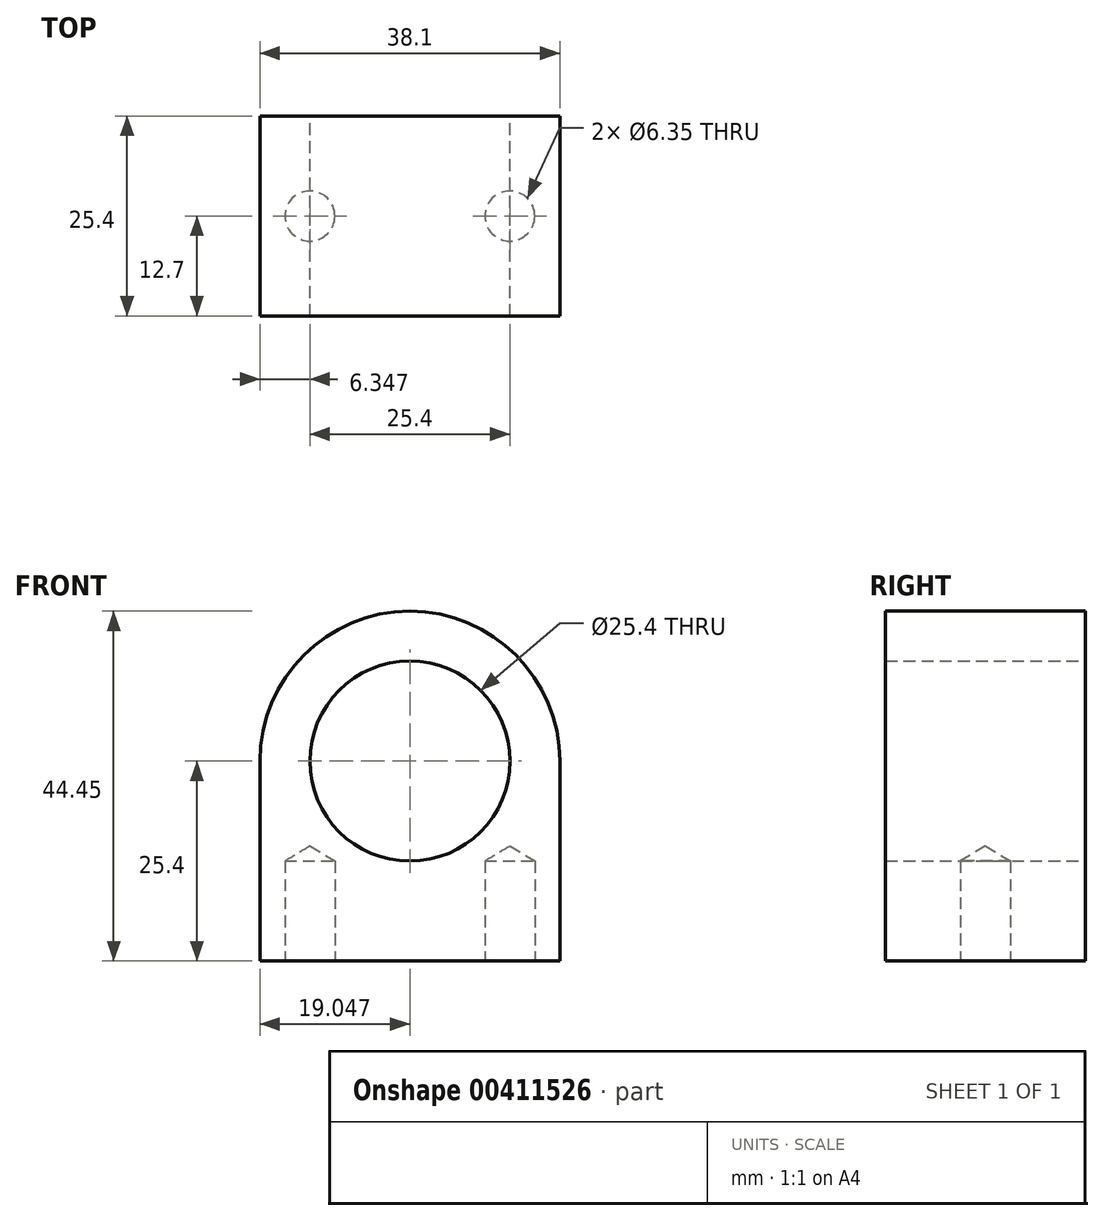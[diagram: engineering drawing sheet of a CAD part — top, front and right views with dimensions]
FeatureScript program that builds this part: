
annotation { "Feature Type Name" : "Feature", "Feature Type Description" : "" }
export const myFeature = defineFeature(function(context is Context, id is Id, definition is map)
    precondition{}
    {
        {
            var Q0;
            Q0=qCreatedBy(makeId("Front.planeOp"),FACE);
            var sketch = newSketch(context, id + "F0", { "sketchPlane" : qUnion([Q0])});
            skLineSegment(sketch, "E0", {"start": v(-22.9, 0) * mm, "end": v(-22.9, -25.4) * mm});
            skLineSegment(sketch, "E1", {"start": v(-22.9, -25.4) * mm, "end": v(15.2, -25.4) * mm});
            skLineSegment(sketch, "E2", {"start": v(15.2, -25.4) * mm, "end": v(15.2, 0) * mm});
            skArc(sketch, "E3", {"start": v(15.2, 0) * mm, "mid": v(-3.84, 19.05) * mm, "end": v(-22.9, 0) * mm});
            skPoint(sketch, "E3.centerSnap0", {"position": v(-3.84, -25.4) * mm});
            skCircle(sketch, "E4", {"center": v(-3.84, 0) * mm, "radius": 12.7 * mm});
            skSolve(sketch);
        }
        {
            var Q0;
            Q0=makeQuery(id+"F0.imprint","IMPRINT",FACE,{"disambiguationData":[TD([[makeQuery(id+"F0.imprint","IMPRINT",EDGE,{"derivedFrom":sQuery(id+"F0.wireOp",EDGE,"E0")}),1.0]])]});
            extrude(context, id + "F1", {"entities" : qUnion([Q0]), "depth" : 25.4 * mm});
        }
        {
            var Q0;
            Q0=makeQuery(id+"F1.opExtrude","SWEPT_FACE",FACE,{"disambiguationData":[OSD([sQuery(id+"F0.wireOp",EDGE,"E1")])]});
            var sketch = newSketch(context, id + "F2", { "sketchPlane" : qUnion([Q0])});
            skLineSegment(sketch, "E5", {"start": v(-3.84, 25.4) * mm, "end": v(-3.84, -8.24) * mm});
            skPoint(sketch, "E5.endSnap0", {"position": v(-3.84, 0) * mm});
            skLineSegment(sketch, "E6", {"start": v(-22.9, 12.7) * mm, "end": v(15.2, 12.7) * mm});
            skCircle(sketch, "E7", {"center": v(8.86, 12.7) * mm, "radius": 3.18 * mm});
            skCircle(sketch, "E8", {"center": v(-16.54, 12.7) * mm, "radius": 3.18 * mm});
            skSolve(sketch);
        }
        {
            var Q0;
            Q0=sQuery(id+"F2.wireOp",VERTEX,"E8.center");
            var Q1;
            Q1=sQuery(id+"F2.wireOp",VERTEX,"E7.center");
            var Q2;
            Q2=makeQuery(id+"F1.opExtrude","SWEPT_BODY",BODY,{"disambiguationData":[OSD([sQuery(id+"F0.wireOp",EDGE,"E0"),sQuery(id+"F0.wireOp",EDGE,"E1"),sQuery(id+"F0.wireOp",EDGE,"E2"),sQuery(id+"F0.wireOp",EDGE,"E3"),sQuery(id+"F0.wireOp",EDGE,"E4")])]});
            hole(context, id + "F3", {"style" : HoleStyle.SIMPLE, "endStyle" : HoleEndStyle.BLIND, "holeDiameter" : 6.35 * mm, "holeDepth" : 12.7 * mm, "isTappedThrough" : true, "tappedDepth" : 12.7 * mm, "tapClearance" : 3, "locations" : qUnion([Q0, Q1]), "scope" : qUnion([Q2])});
        }
    });
